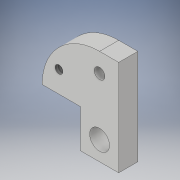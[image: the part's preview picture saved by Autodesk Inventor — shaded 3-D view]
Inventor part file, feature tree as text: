
AUTODESK INVENTOR PART (.ipt)
format: ipt  version: 2019 (Build 230136000, 136)  size: 130,560 bytes
history: native  units: in
note: dims shown in document units (in); Inventor stores cm internally (conversion verified against a paired STEP export)
features: sketch x4, hole x3, extrude x1, fillet x1
ambient origin geometry x8: Origin, YZ Plane, XZ Plane, XY Plane, X Axis, Y Axis, Z Axis, Center Point
bodies: Solid1 (feature_tree)
feature tree (9):
  extrude  "Extrusion1"  Depth=0.75in
  fillet  "Fillet1"  Radius=0.75in
  hole  "Hole1"  [1 undecoded]
  hole  "Hole2"  [1 undecoded]
  hole  "Hole3"  [1 undecoded]
  sketch  "Sketch1"  dims[d1=1.25in d2=1.0in d3=0.75in]
  sketch  "Sketch2"  dims[d4=0.5in d5=0.5in]
  sketch  "Sketch3"  dims[d8=0.25in d9=0.0in d10=0.75in]
  sketch  "Sketch4"  dims[d11=0.25in d12=0.25in d13=0.26in d14=0.276in d15=0.375in d16=0.25in d17=0.5635in d18=1.0in d19=0.8108in d20=0.25in d21=0.25in d22=0.14in d23=0.224in d24=0.375in d25=0.25in d26=0.5635in d27=0.349in d28=0.8108in d29=1.5in d30=45.0deg d31=0.104in d32=0.276in d33=0.375in d34=0.25in d35=0.5635in d36=0.432in d37=0.8108in]
note: 3 required parameter values undecoded (feature->parameter linkage not recoverable at this tier; creation-order binding heuristic only, values carry confidence <= 0.55)
